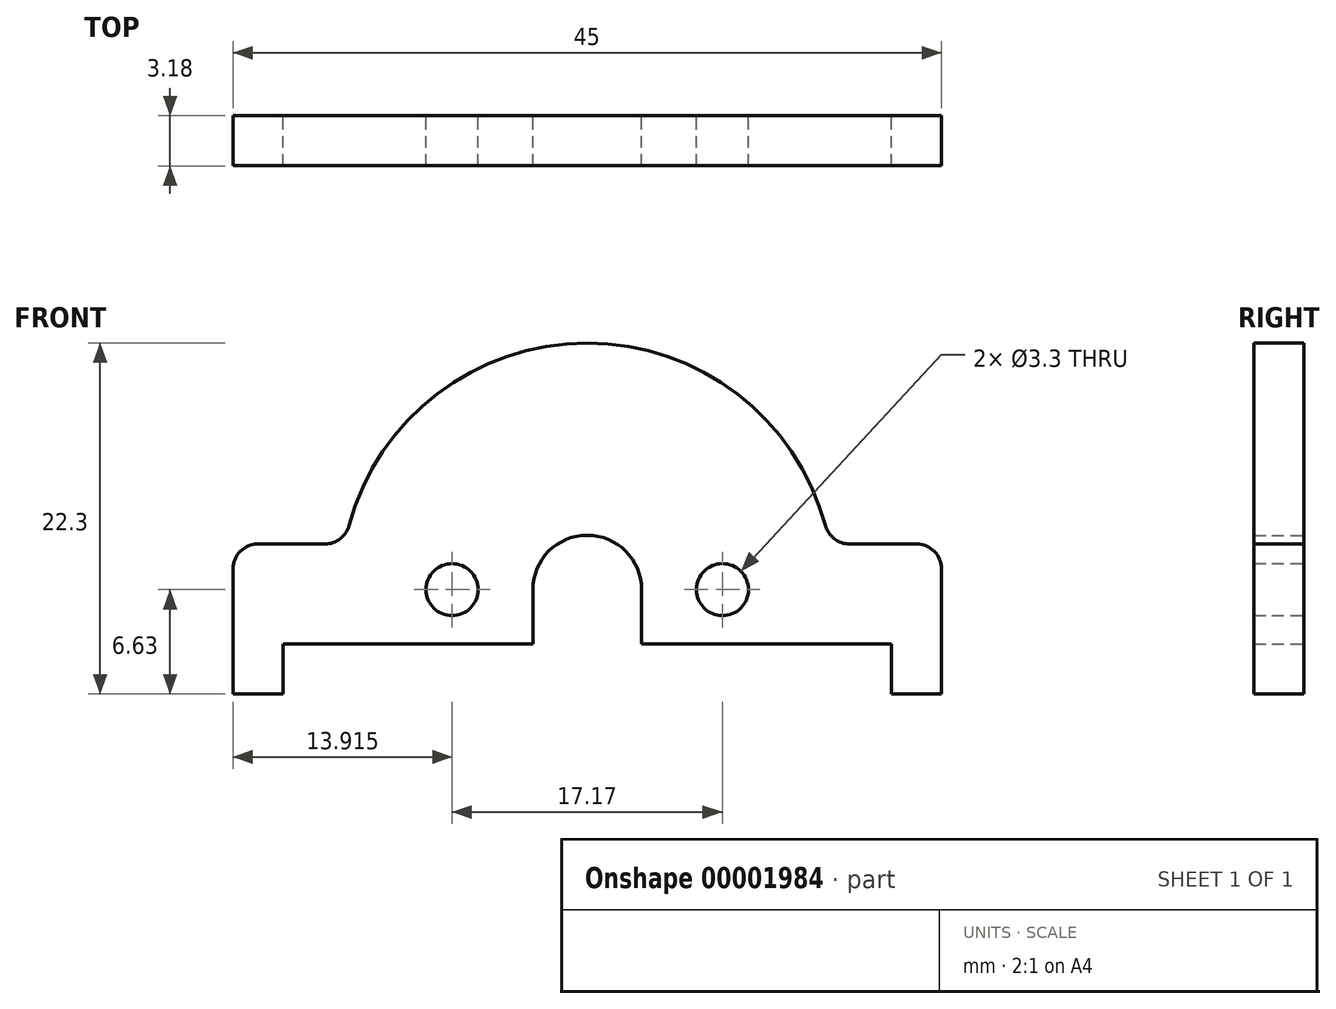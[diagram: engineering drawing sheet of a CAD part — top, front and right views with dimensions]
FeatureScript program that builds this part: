
annotation { "Feature Type Name" : "Feature", "Feature Type Description" : "" }
export const myFeature = defineFeature(function(context is Context, id is Id, definition is map)
    precondition{}
    {
        {
            var Q0;
            Q0=qCreatedBy(makeId("Front.planeOp"),FACE);
            var sketch = newSketch(context, id + "F0", { "sketchPlane" : qUnion([Q0])});
            skArc(sketch, "E0.0", {"start": v(3.45, 0) * mm, "mid": v(0, 3.45) * mm, "end": v(-3.45, 0) * mm});
            skCircle(sketch, "E1.0", {"center": v(-8.59, 0) * mm, "radius": 1.65 * mm});
            skCircle(sketch, "E2.0.MirrorC", {"center": v(8.59, 0) * mm, "radius": 1.65 * mm});
            skCircle(sketch, "E3.0", {"center": v(0, 0) * mm, "radius": 12.5 * mm, "construction": true});
            skPoint(sketch, "E4", {"position": v(0, 12.5) * mm});
            skLineSegment(sketch, "E5", {"start": v(-19.33, -3.45) * mm, "end": v(-3.45, -3.45) * mm});
            skLineSegment(sketch, "E6", {"start": v(-3.45, 0) * mm, "end": v(-3.45, -3.45) * mm});
            skLineSegment(sketch, "E7", {"start": v(3.45, 0) * mm, "end": v(3.45, -3.45) * mm});
            skLineSegment(sketch, "E8", {"start": v(-22.5, -3.45) * mm, "end": v(-22.5, 1.3) * mm});
            skLineSegment(sketch, "E9", {"start": v(-20.92, 2.9) * mm, "end": v(-16.66, 2.9) * mm});
            skArc(sketch, "E10", {"start": v(0, 15.67) * mm, "mid": v(-9.53, 12.43) * mm, "end": v(-15.13, 4.07) * mm});
            skPoint(sketch, "E11.visualSharp", {"position": v(-15.4, 2.9) * mm});
            skArc(sketch, "E11.filletArc", {"start": v(-16.66, 2.9) * mm, "mid": v(-15.7, 3.22) * mm, "end": v(-15.13, 4.07) * mm});
            skPoint(sketch, "E12.visualSharp", {"position": v(-22.5, 2.9) * mm});
            skArc(sketch, "E12.filletArc", {"start": v(-20.92, 2.9) * mm, "mid": v(-22.04, 2.43) * mm, "end": v(-22.5, 1.3) * mm});
            skArc(sketch, "E13.0.MirrorCS", {"start": v(16.66, 2.9) * mm, "mid": v(15.7, 3.22) * mm, "end": v(15.13, 4.07) * mm});
            skLineSegment(sketch, "E13.1.MirrorCS", {"start": v(19.33, -3.45) * mm, "end": v(3.45, -3.45) * mm});
            skLineSegment(sketch, "E13.2.MirrorCS", {"start": v(22.5, -3.45) * mm, "end": v(22.5, 1.3) * mm});
            skLineSegment(sketch, "E13.3.MirrorCS", {"start": v(20.92, 2.9) * mm, "end": v(16.66, 2.9) * mm});
            skPoint(sketch, "E13.4.MirrorP", {"position": v(22.5, 2.9) * mm});
            skArc(sketch, "E13.5.MirrorCS", {"start": v(20.92, 2.9) * mm, "mid": v(22.04, 2.43) * mm, "end": v(22.5, 1.3) * mm});
            skPoint(sketch, "E13.6.MirrorP", {"position": v(15.4, 2.9) * mm});
            skLineSegment(sketch, "E14", {"start": v(-22.5, -3.45) * mm, "end": v(-22.5, -6.63) * mm});
            skLineSegment(sketch, "E15", {"start": v(-22.5, -6.63) * mm, "end": v(-19.33, -6.63) * mm});
            skLineSegment(sketch, "E16", {"start": v(-19.33, -6.63) * mm, "end": v(-19.33, -3.45) * mm});
            skArc(sketch, "E17.0.MirrorCS", {"start": v(0, 15.67) * mm, "mid": v(9.53, 12.43) * mm, "end": v(15.13, 4.07) * mm});
            skLineSegment(sketch, "E17.2.MirrorCS", {"start": v(22.5, -3.45) * mm, "end": v(22.5, -6.63) * mm});
            skLineSegment(sketch, "E17.5.MirrorCS", {"start": v(19.33, -6.63) * mm, "end": v(19.33, -3.45) * mm});
            skLineSegment(sketch, "E17.6.MirrorCS", {"start": v(22.5, -6.63) * mm, "end": v(19.33, -6.63) * mm});
            skSolve(sketch);
        }
        {
            var Q0;
            Q0=makeQuery(id+"F0.imprint","IMPRINT",FACE,{"disambiguationData":[TD([[makeQuery(id+"F0.imprint","IMPRINT",EDGE,{"derivedFrom":sQuery(id+"F0.wireOp",EDGE,"E0.0")}),-1.0]])]});
            extrude(context, id + "F1", {"entities" : qUnion([Q0]), "depth" : 3.17 * mm});
        }
    });
